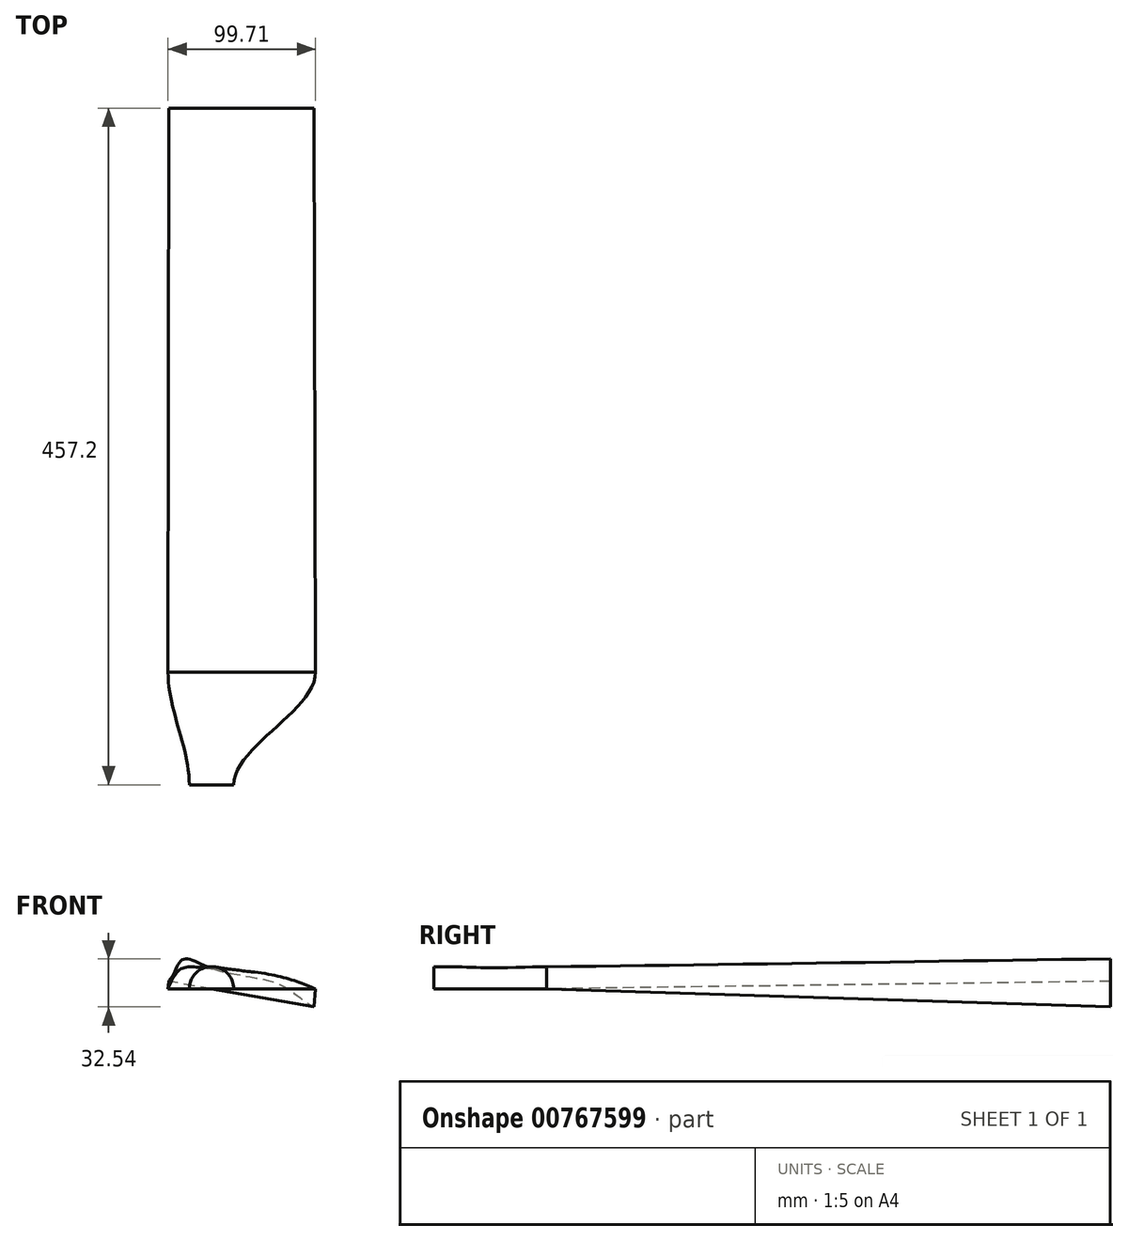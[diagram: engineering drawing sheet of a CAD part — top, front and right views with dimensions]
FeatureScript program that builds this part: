
annotation { "Feature Type Name" : "Feature", "Feature Type Description" : "" }
export const myFeature = defineFeature(function(context is Context, id is Id, definition is map)
    precondition{}
    {
        {
            var Q0;
            Q0=qCreatedBy(makeId("Front.planeOp"),FACE);
            var sketch = newSketch(context, id + "F0", { "sketchPlane" : qUnion([Q0])});
            skPoint(sketch, "E0", {"position": v(-29.4, 0) * mm});
            skPoint(sketch, "E1", {"position": v(-21.05, 13.14) * mm});
            skPoint(sketch, "E2", {"position": v(-4.34, 14.22) * mm});
            skPoint(sketch, "E3", {"position": v(41.87, 9.3) * mm});
            skPoint(sketch, "E4", {"position": v(70.3, 0) * mm});
            skFitSpline(sketch, "E5", {"points": [v(-29.4, 0) * mm, v(-21.05, 13.14) * mm, v(-4.34, 14.22) * mm, v(41.87, 9.3) * mm, v(70.3, 0) * mm], "startDerivative": vector(36.02, 83.06) * mm, "endDerivative": vector(94.2, -39.14) * mm});
            skFitSpline(sketch, "E6", {"points": [v(70.3, 0) * mm, v(-29.4, 0) * mm], "startDerivative": vector(-99.7, 0) * mm, "endDerivative": vector(-99.7, 0) * mm});
            skSolve(sketch);
        }
        {
            var Q0;
            Q0=qCreatedBy(makeId("Front.planeOp"),FACE);
            cPlane(context, id + "F1", {"entities" : qUnion([Q0]), "cplaneType" : CPlaneType.OFFSET, "offset" : 76.2 * mm, "width" : 152.4 * mm, "height" : 152.4 * mm});
        }
        {
            var Q0;
            Q0=qCreatedBy(id+"F1.planeOp",FACE);
            var sketch = newSketch(context, id + "F2", { "sketchPlane" : qUnion([Q0])});
            skArc(sketch, "E7", {"start": v(15.02, 0) * mm, "mid": v(0, 15.02) * mm, "end": v(-15.02, 0) * mm});
            skLineSegment(sketch, "E8", {"start": v(-15.02, 0) * mm, "end": v(15.02, 0) * mm});
            skSolve(sketch);
        }
        {
            var Q0;
            Q0=makeQuery(id+"F0.imprint","IMPRINT",FACE,{"disambiguationData":[TD([[makeQuery(id+"F0.imprint","IMPRINT",EDGE,{"derivedFrom":sQuery(id+"F0.wireOp",EDGE,"E5")}),-1.0]])]});
            var Q1;
            Q1=makeQuery(id+"F2.imprint","IMPRINT",FACE,{"disambiguationData":[TD([[makeQuery(id+"F2.imprint","IMPRINT",EDGE,{"derivedFrom":sQuery(id+"F2.wireOp",EDGE,"E7")}),1.0]])]});
            loft(context, id + "F3", {"startCondition" : LoftEndDerivativeType.NORMAL_TO_PROFILE, "startMagnitude" : 1, "endCondition" : LoftEndDerivativeType.NORMAL_TO_PROFILE, "endMagnitude" : 1, "sheetProfilesArray" : [{ "sheetProfileEntities" : qUnion([Q0]) }, { "sheetProfileEntities" : qUnion([Q1]) }]});
        }
        {
            var Q0;
            Q0=qCreatedBy(makeId("Front.planeOp"),FACE);
            cPlane(context, id + "F4", {"entities" : qUnion([Q0]), "cplaneType" : CPlaneType.OFFSET, "offset" : 381 * mm, "oppositeDirection" : true, "width" : 152.4 * mm, "height" : 152.4 * mm});
        }
        {
            var Q0;
            Q0=qCreatedBy(id+"F4.planeOp",FACE);
            var sketch = newSketch(context, id + "F5", { "sketchPlane" : qUnion([Q0])});
            skFitSpline(sketch, "E9.0", {"points": [v(-28.95, 5.1) * mm, v(-25.72, 10) * mm, v(-19.14, 19.95) * mm, v(-0.74, 14) * mm, v(44.2, 3.78) * mm, v(61.53, -7.28) * mm, v(69.24, -12.2) * mm]});
            skFitSpline(sketch, "E9.1", {"points": [v(69.24, -12.2) * mm, v(36.51, -6.44) * mm, v(3.78, -0.67) * mm, v(-28.95, 5.1) * mm]});
            skSolve(sketch);
        }
        {
            var Q1;
            Q1=makeQuery(id+"F5.imprint","IMPRINT",FACE,{"disambiguationData":[TD([[makeQuery(id+"F5.imprint","IMPRINT",EDGE,{"derivedFrom":sQuery(id+"F5.wireOp",EDGE,"E9.0")}),-1.0]])]});
            var Q2;
            Q2=makeQuery(id+"F0.imprint","IMPRINT",FACE,{"disambiguationData":[TD([[makeQuery(id+"F0.imprint","IMPRINT",EDGE,{"derivedFrom":sQuery(id+"F0.wireOp",EDGE,"E5")}),-1.0]])]});
            loft(context, id + "F6", {"operationType" : NewBodyOperationType.ADD, "sheetProfilesArray" : [{ "sheetProfileEntities" : qUnion([Q1]) }, { "sheetProfileEntities" : qUnion([Q2]) }]});
        }
        {
            var Q0;
            Q0=qCreatedBy(id+"F4.planeOp",FACE);
            cPlane(context, id + "F7", {"entities" : qUnion([Q0]), "cplaneType" : CPlaneType.OFFSET, "offset" : 25.4 * mm, "oppositeDirection" : true, "width" : 152.4 * mm, "height" : 152.4 * mm});
        }
        {
            var Q0;
            Q0=qCreatedBy(id+"F7.planeOp",FACE);
            var sketch = newSketch(context, id + "F8", { "sketchPlane" : qUnion([Q0])});
            skFitSpline(sketch, "E10.0", {"points": [v(-28.95, 5.1) * mm, v(3.78, -0.67) * mm, v(36.51, -6.44) * mm, v(69.24, -12.2) * mm]});
            skSolve(sketch);
        }
        {
            var Q0;
            {var subQ0=sQuery(id+"F5.wireOp",EDGE,"E9.0");var subQ1=sQuery(id+"F5.wireOp",EDGE,"E9.1");var subQ2=sQuery(id+"F0.wireOp",EDGE,"E5");var subQ3=sQuery(id+"F0.wireOp",EDGE,"E6");Q0=makeQuery(id+"F6.opLoft","SWEPT_FACE",FACE,{"disambiguationData":[OSD([subQ2,subQ3,subQ0,subQ1]),TDD([makeQuery(id+"F0.imprint","INTERSECT",VERTEX,{"disambiguationData":[OD(0.0)],"derivedFrom":[subQ2,subQ3]}),makeQuery(id+"F0.imprint","INTERSECT",VERTEX,{"disambiguationData":[OD(1.0)],"derivedFrom":[subQ2,subQ3]}),makeQuery(id+"F0.imprint","IMPRINT",EDGE,{"derivedFrom":subQ2}),makeQuery(id+"F5.imprint","INTERSECT",VERTEX,{"disambiguationData":[OD(0.0)],"derivedFrom":[subQ0,subQ1]}),makeQuery(id+"F5.imprint","INTERSECT",VERTEX,{"disambiguationData":[OD(1.0)],"derivedFrom":[subQ0,subQ1]}),makeQuery(id+"F5.imprint","IMPRINT",EDGE,{"derivedFrom":subQ0})])]});}
            var Q1;
            {var subQ0=sQuery(id+"F5.wireOp",EDGE,"E9.0");var subQ1=sQuery(id+"F5.wireOp",EDGE,"E9.1");Q1=makeQuery(id+"F6.opLoft","MID_CAP_EDGE",EDGE,{"disambiguationData":[OSD([subQ0,subQ1]),TDD([makeQuery(id+"F5.imprint","INTERSECT",VERTEX,{"disambiguationData":[OD(0.0)],"derivedFrom":[subQ0,subQ1]}),makeQuery(id+"F5.imprint","INTERSECT",VERTEX,{"disambiguationData":[OD(1.0)],"derivedFrom":[subQ0,subQ1]}),makeQuery(id+"F5.imprint","IMPRINT",EDGE,{"derivedFrom":subQ0})])],"capPos":0.0});}
            var Q2;
            Q2=sQuery(id+"F8.wireOp",EDGE,"E10.0");
            loft(context, id + "F9", {"bodyType" : ToolBodyType.SURFACE, "sheetProfilesArray" : [{ "sheetProfileEntities" : qUnion([Q0]) }], "wireProfilesArray" : [{ "wireProfileEntities" : qUnion([Q1]) }, { "wireProfileEntities" : qUnion([Q2]) }]});
        }
    });
